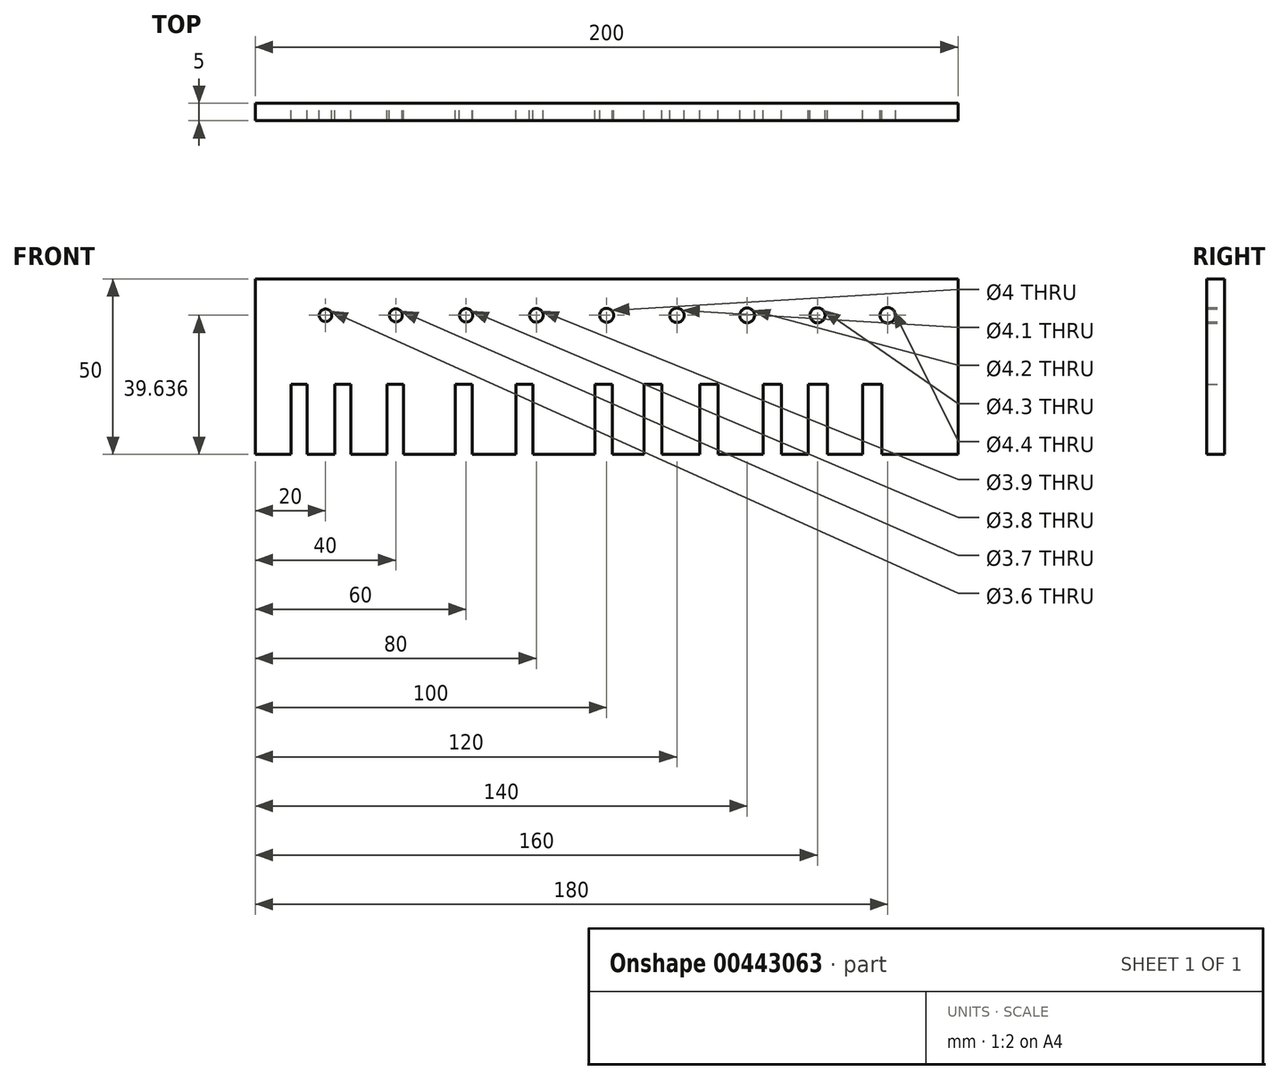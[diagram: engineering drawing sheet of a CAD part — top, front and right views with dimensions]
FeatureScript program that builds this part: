
annotation { "Feature Type Name" : "Feature", "Feature Type Description" : "" }
export const myFeature = defineFeature(function(context is Context, id is Id, definition is map)
    precondition{}
    {
        {
            var Q0;
            Q0=qCreatedBy(makeId("Front.planeOp"),FACE);
            var sketch = newSketch(context, id + "F0", { "sketchPlane" : qUnion([Q0])});
            skLineSegment(sketch, "E0.bottom", {"start": v(100, 25) * mm, "end": v(-100, 25) * mm});
            skLineSegment(sketch, "E0.top", {"start": v(100, -25) * mm, "end": v(-100, -25) * mm});
            skLineSegment(sketch, "E0.left", {"start": v(100, 25) * mm, "end": v(100, -25) * mm});
            skLineSegment(sketch, "E0.right", {"start": v(-100, 25) * mm, "end": v(-100, -25) * mm});
            skPoint(sketch, "E0.middle", {"position": v(0, 0) * mm});
            skLineSegment(sketch, "E1.bottom", {"start": v(-3.33, -25) * mm, "end": v(1.67, -25) * mm});
            skLineSegment(sketch, "E1.top", {"start": v(-3.33, -5) * mm, "end": v(1.67, -5) * mm});
            skLineSegment(sketch, "E1.left", {"start": v(-3.33, -25) * mm, "end": v(-3.33, -5) * mm});
            skLineSegment(sketch, "E1.right", {"start": v(1.67, -25) * mm, "end": v(1.67, -5) * mm});
            skLineSegment(sketch, "E2.bottom", {"start": v(-20.96, -25) * mm, "end": v(-25.86, -25) * mm});
            skLineSegment(sketch, "E2.top", {"start": v(-20.96, -5) * mm, "end": v(-25.86, -5) * mm});
            skLineSegment(sketch, "E2.left", {"start": v(-20.96, -25) * mm, "end": v(-20.96, -5) * mm});
            skLineSegment(sketch, "E2.right", {"start": v(-25.86, -25) * mm, "end": v(-25.86, -5) * mm});
            skLineSegment(sketch, "E3.bottom", {"start": v(-38.22, -25) * mm, "end": v(-43.02, -25) * mm});
            skLineSegment(sketch, "E3.top", {"start": v(-38.22, -5) * mm, "end": v(-43.02, -5) * mm});
            skLineSegment(sketch, "E3.left", {"start": v(-38.22, -25) * mm, "end": v(-38.22, -5) * mm});
            skLineSegment(sketch, "E3.right", {"start": v(-43.02, -25) * mm, "end": v(-43.02, -5) * mm});
            skLineSegment(sketch, "E4.bottom", {"start": v(-57.85, -25) * mm, "end": v(-62.55, -25) * mm});
            skLineSegment(sketch, "E4.top", {"start": v(-57.85, -5) * mm, "end": v(-62.55, -5) * mm});
            skLineSegment(sketch, "E4.left", {"start": v(-57.85, -25) * mm, "end": v(-57.85, -5) * mm});
            skLineSegment(sketch, "E4.right", {"start": v(-62.55, -25) * mm, "end": v(-62.55, -5) * mm});
            skLineSegment(sketch, "E5.bottom", {"start": v(-72.75, -25) * mm, "end": v(-77.35, -25) * mm});
            skLineSegment(sketch, "E5.top", {"start": v(-72.75, -5) * mm, "end": v(-77.35, -5) * mm});
            skLineSegment(sketch, "E5.left", {"start": v(-72.75, -25) * mm, "end": v(-72.75, -5) * mm});
            skLineSegment(sketch, "E5.right", {"start": v(-77.35, -25) * mm, "end": v(-77.35, -5) * mm});
            skLineSegment(sketch, "E6.bottom", {"start": v(-85.3, -25) * mm, "end": v(-89.8, -25) * mm});
            skLineSegment(sketch, "E6.top", {"start": v(-85.3, -5) * mm, "end": v(-89.8, -5) * mm});
            skLineSegment(sketch, "E6.left", {"start": v(-85.3, -25) * mm, "end": v(-85.3, -5) * mm});
            skLineSegment(sketch, "E6.right", {"start": v(-89.8, -25) * mm, "end": v(-89.8, -5) * mm});
            skLineSegment(sketch, "E7.bottom", {"start": v(10.61, -25) * mm, "end": v(15.71, -25) * mm});
            skLineSegment(sketch, "E7.top", {"start": v(10.61, -5) * mm, "end": v(15.71, -5) * mm});
            skLineSegment(sketch, "E7.left", {"start": v(10.61, -25) * mm, "end": v(10.61, -5) * mm});
            skLineSegment(sketch, "E7.right", {"start": v(15.71, -25) * mm, "end": v(15.71, -5) * mm});
            skLineSegment(sketch, "E8.bottom", {"start": v(26.49, -25) * mm, "end": v(31.69, -25) * mm});
            skLineSegment(sketch, "E8.top", {"start": v(26.49, -5) * mm, "end": v(31.69, -5) * mm});
            skLineSegment(sketch, "E8.left", {"start": v(26.49, -25) * mm, "end": v(26.49, -5) * mm});
            skLineSegment(sketch, "E8.right", {"start": v(31.69, -25) * mm, "end": v(31.69, -5) * mm});
            skLineSegment(sketch, "E9.bottom", {"start": v(44.5, -25) * mm, "end": v(49.8, -25) * mm});
            skLineSegment(sketch, "E9.top", {"start": v(44.5, -5) * mm, "end": v(49.8, -5) * mm});
            skLineSegment(sketch, "E9.left", {"start": v(44.5, -25) * mm, "end": v(44.5, -5) * mm});
            skLineSegment(sketch, "E9.right", {"start": v(49.8, -25) * mm, "end": v(49.8, -5) * mm});
            skLineSegment(sketch, "E10.bottom", {"start": v(57.38, -25) * mm, "end": v(62.78, -25) * mm});
            skLineSegment(sketch, "E10.top", {"start": v(57.38, -5) * mm, "end": v(62.78, -5) * mm});
            skLineSegment(sketch, "E10.left", {"start": v(57.38, -25) * mm, "end": v(57.38, -5) * mm});
            skLineSegment(sketch, "E10.right", {"start": v(62.78, -25) * mm, "end": v(62.78, -5) * mm});
            skLineSegment(sketch, "E11.bottom", {"start": v(72.83, -25) * mm, "end": v(78.33, -25) * mm});
            skLineSegment(sketch, "E11.top", {"start": v(72.83, -5) * mm, "end": v(78.33, -5) * mm});
            skLineSegment(sketch, "E11.left", {"start": v(72.83, -25) * mm, "end": v(72.83, -5) * mm});
            skLineSegment(sketch, "E11.right", {"start": v(78.33, -25) * mm, "end": v(78.33, -5) * mm});
            skSolve(sketch);
        }
        {
            var Q0;
            Q0=makeQuery(id+"F0.imprint","IMPRINT",FACE,{"disambiguationData":[TD([[makeQuery(id+"F0.imprint","IMPRINT",EDGE,{"derivedFrom":sQuery(id+"F0.wireOp",EDGE,"E0.bottom")}),1.0]])]});
            extrude(context, id + "F1", {"entities" : qUnion([Q0]), "depth" : 5 * mm});
        }
        {
            var Q0;
            Q0=qCreatedBy(makeId("Front.planeOp"),FACE);
            var sketch = newSketch(context, id + "F2", { "sketchPlane" : qUnion([Q0])});
            skPoint(sketch, "E12", {"position": v(0, 14.64) * mm});
            skPoint(sketch, "E13.1.0.0", {"position": v(20, 14.64) * mm});
            skPoint(sketch, "E13.2.0.0", {"position": v(40, 14.64) * mm});
            skPoint(sketch, "E13.3.0.0", {"position": v(60, 14.64) * mm});
            skPoint(sketch, "E13.4.0.0", {"position": v(80, 14.64) * mm});
            skLineSegment(sketch, "E13.direction1", {"start": v(0, 14.64) * mm, "end": v(20, 14.64) * mm, "construction": true});
            skPoint(sketch, "E14.1.0.0", {"position": v(-20, 14.64) * mm});
            skPoint(sketch, "E14.2.0.0", {"position": v(-40, 14.64) * mm});
            skPoint(sketch, "E14.3.0.0", {"position": v(-60, 14.64) * mm});
            skPoint(sketch, "E14.4.0.0", {"position": v(-80, 14.64) * mm});
            skLineSegment(sketch, "E14.direction1", {"start": v(0, 14.64) * mm, "end": v(-20, 14.64) * mm, "construction": true});
            skSolve(sketch);
        }
        {
            var Q0;
            Q0=sQuery(id+"F2.wireOp",VERTEX,"E12");
            var Q1;
            Q1=makeQuery(id+"F1.opExtrude","SWEPT_BODY",BODY,{"disambiguationData":[OSD([sQuery(id+"F0.wireOp",EDGE,"E0.bottom"),sQuery(id+"F0.wireOp",EDGE,"E0.top"),sQuery(id+"F0.wireOp",EDGE,"E0.left"),sQuery(id+"F0.wireOp",EDGE,"E0.right"),sQuery(id+"F0.wireOp",EDGE,"E1.top"),sQuery(id+"F0.wireOp",EDGE,"E1.left"),sQuery(id+"F0.wireOp",EDGE,"E1.right"),sQuery(id+"F0.wireOp",EDGE,"E2.top"),sQuery(id+"F0.wireOp",EDGE,"E2.left"),sQuery(id+"F0.wireOp",EDGE,"E2.right"),sQuery(id+"F0.wireOp",EDGE,"E3.top"),sQuery(id+"F0.wireOp",EDGE,"E3.left"),sQuery(id+"F0.wireOp",EDGE,"E3.right"),sQuery(id+"F0.wireOp",EDGE,"E4.top"),sQuery(id+"F0.wireOp",EDGE,"E4.left"),sQuery(id+"F0.wireOp",EDGE,"E4.right"),sQuery(id+"F0.wireOp",EDGE,"E5.top"),sQuery(id+"F0.wireOp",EDGE,"E5.left"),sQuery(id+"F0.wireOp",EDGE,"E5.right"),sQuery(id+"F0.wireOp",EDGE,"E6.top"),sQuery(id+"F0.wireOp",EDGE,"E6.left"),sQuery(id+"F0.wireOp",EDGE,"E6.right"),sQuery(id+"F0.wireOp",EDGE,"E7.top"),sQuery(id+"F0.wireOp",EDGE,"E7.left"),sQuery(id+"F0.wireOp",EDGE,"E7.right"),sQuery(id+"F0.wireOp",EDGE,"E8.top"),sQuery(id+"F0.wireOp",EDGE,"E8.left"),sQuery(id+"F0.wireOp",EDGE,"E8.right"),sQuery(id+"F0.wireOp",EDGE,"E9.top"),sQuery(id+"F0.wireOp",EDGE,"E9.left"),sQuery(id+"F0.wireOp",EDGE,"E9.right"),sQuery(id+"F0.wireOp",EDGE,"E10.top"),sQuery(id+"F0.wireOp",EDGE,"E10.left"),sQuery(id+"F0.wireOp",EDGE,"E10.right"),sQuery(id+"F0.wireOp",EDGE,"E11.top"),sQuery(id+"F0.wireOp",EDGE,"E11.left"),sQuery(id+"F0.wireOp",EDGE,"E11.right")])]});
            hole(context, id + "F3", {"style" : HoleStyle.SIMPLE, "endStyle" : HoleEndStyle.THROUGH, "oppositeDirection" : true, "holeDiameter" : 4 * mm, "isTappedThrough" : true, "tappedDepth" : 12 * mm, "tapClearance" : 3, "locations" : qUnion([Q0]), "scope" : qUnion([Q1])});
        }
        {
            var Q0;
            Q0=sQuery(id+"F2.wireOp",VERTEX,"E13.1.0.0");
            var Q1;
            Q1=makeQuery(id+"F1.opExtrude","SWEPT_BODY",BODY,{"disambiguationData":[OSD([sQuery(id+"F0.wireOp",EDGE,"E0.bottom"),sQuery(id+"F0.wireOp",EDGE,"E0.top"),sQuery(id+"F0.wireOp",EDGE,"E0.left"),sQuery(id+"F0.wireOp",EDGE,"E0.right"),sQuery(id+"F0.wireOp",EDGE,"E1.top"),sQuery(id+"F0.wireOp",EDGE,"E1.left"),sQuery(id+"F0.wireOp",EDGE,"E1.right"),sQuery(id+"F0.wireOp",EDGE,"E2.top"),sQuery(id+"F0.wireOp",EDGE,"E2.left"),sQuery(id+"F0.wireOp",EDGE,"E2.right"),sQuery(id+"F0.wireOp",EDGE,"E3.top"),sQuery(id+"F0.wireOp",EDGE,"E3.left"),sQuery(id+"F0.wireOp",EDGE,"E3.right"),sQuery(id+"F0.wireOp",EDGE,"E4.top"),sQuery(id+"F0.wireOp",EDGE,"E4.left"),sQuery(id+"F0.wireOp",EDGE,"E4.right"),sQuery(id+"F0.wireOp",EDGE,"E5.top"),sQuery(id+"F0.wireOp",EDGE,"E5.left"),sQuery(id+"F0.wireOp",EDGE,"E5.right"),sQuery(id+"F0.wireOp",EDGE,"E6.top"),sQuery(id+"F0.wireOp",EDGE,"E6.left"),sQuery(id+"F0.wireOp",EDGE,"E6.right"),sQuery(id+"F0.wireOp",EDGE,"E7.top"),sQuery(id+"F0.wireOp",EDGE,"E7.left"),sQuery(id+"F0.wireOp",EDGE,"E7.right"),sQuery(id+"F0.wireOp",EDGE,"E8.top"),sQuery(id+"F0.wireOp",EDGE,"E8.left"),sQuery(id+"F0.wireOp",EDGE,"E8.right"),sQuery(id+"F0.wireOp",EDGE,"E9.top"),sQuery(id+"F0.wireOp",EDGE,"E9.left"),sQuery(id+"F0.wireOp",EDGE,"E9.right"),sQuery(id+"F0.wireOp",EDGE,"E10.top"),sQuery(id+"F0.wireOp",EDGE,"E10.left"),sQuery(id+"F0.wireOp",EDGE,"E10.right"),sQuery(id+"F0.wireOp",EDGE,"E11.top"),sQuery(id+"F0.wireOp",EDGE,"E11.left"),sQuery(id+"F0.wireOp",EDGE,"E11.right")])]});
            hole(context, id + "F4", {"style" : HoleStyle.SIMPLE, "endStyle" : HoleEndStyle.THROUGH, "oppositeDirection" : true, "holeDiameter" : 4.1 * mm, "isTappedThrough" : true, "tappedDepth" : 12 * mm, "tapClearance" : 3, "locations" : qUnion([Q0]), "scope" : qUnion([Q1])});
        }
        {
            var Q0;
            Q0=sQuery(id+"F2.wireOp",VERTEX,"E13.2.0.0");
            var Q1;
            Q1=makeQuery(id+"F1.opExtrude","SWEPT_BODY",BODY,{"disambiguationData":[OSD([sQuery(id+"F0.wireOp",EDGE,"E0.bottom"),sQuery(id+"F0.wireOp",EDGE,"E0.top"),sQuery(id+"F0.wireOp",EDGE,"E0.left"),sQuery(id+"F0.wireOp",EDGE,"E0.right"),sQuery(id+"F0.wireOp",EDGE,"E1.top"),sQuery(id+"F0.wireOp",EDGE,"E1.left"),sQuery(id+"F0.wireOp",EDGE,"E1.right"),sQuery(id+"F0.wireOp",EDGE,"E2.top"),sQuery(id+"F0.wireOp",EDGE,"E2.left"),sQuery(id+"F0.wireOp",EDGE,"E2.right"),sQuery(id+"F0.wireOp",EDGE,"E3.top"),sQuery(id+"F0.wireOp",EDGE,"E3.left"),sQuery(id+"F0.wireOp",EDGE,"E3.right"),sQuery(id+"F0.wireOp",EDGE,"E4.top"),sQuery(id+"F0.wireOp",EDGE,"E4.left"),sQuery(id+"F0.wireOp",EDGE,"E4.right"),sQuery(id+"F0.wireOp",EDGE,"E5.top"),sQuery(id+"F0.wireOp",EDGE,"E5.left"),sQuery(id+"F0.wireOp",EDGE,"E5.right"),sQuery(id+"F0.wireOp",EDGE,"E6.top"),sQuery(id+"F0.wireOp",EDGE,"E6.left"),sQuery(id+"F0.wireOp",EDGE,"E6.right"),sQuery(id+"F0.wireOp",EDGE,"E7.top"),sQuery(id+"F0.wireOp",EDGE,"E7.left"),sQuery(id+"F0.wireOp",EDGE,"E7.right"),sQuery(id+"F0.wireOp",EDGE,"E8.top"),sQuery(id+"F0.wireOp",EDGE,"E8.left"),sQuery(id+"F0.wireOp",EDGE,"E8.right"),sQuery(id+"F0.wireOp",EDGE,"E9.top"),sQuery(id+"F0.wireOp",EDGE,"E9.left"),sQuery(id+"F0.wireOp",EDGE,"E9.right"),sQuery(id+"F0.wireOp",EDGE,"E10.top"),sQuery(id+"F0.wireOp",EDGE,"E10.left"),sQuery(id+"F0.wireOp",EDGE,"E10.right"),sQuery(id+"F0.wireOp",EDGE,"E11.top"),sQuery(id+"F0.wireOp",EDGE,"E11.left"),sQuery(id+"F0.wireOp",EDGE,"E11.right")])]});
            hole(context, id + "F5", {"style" : HoleStyle.SIMPLE, "endStyle" : HoleEndStyle.THROUGH, "oppositeDirection" : true, "holeDiameter" : 4.2 * mm, "isTappedThrough" : true, "tappedDepth" : 12 * mm, "tapClearance" : 3, "locations" : qUnion([Q0]), "scope" : qUnion([Q1])});
        }
        {
            var Q0;
            Q0=sQuery(id+"F2.wireOp",VERTEX,"E13.3.0.0");
            var Q1;
            Q1=makeQuery(id+"F1.opExtrude","SWEPT_BODY",BODY,{"disambiguationData":[OSD([sQuery(id+"F0.wireOp",EDGE,"E0.bottom"),sQuery(id+"F0.wireOp",EDGE,"E0.top"),sQuery(id+"F0.wireOp",EDGE,"E0.left"),sQuery(id+"F0.wireOp",EDGE,"E0.right"),sQuery(id+"F0.wireOp",EDGE,"E1.top"),sQuery(id+"F0.wireOp",EDGE,"E1.left"),sQuery(id+"F0.wireOp",EDGE,"E1.right"),sQuery(id+"F0.wireOp",EDGE,"E2.top"),sQuery(id+"F0.wireOp",EDGE,"E2.left"),sQuery(id+"F0.wireOp",EDGE,"E2.right"),sQuery(id+"F0.wireOp",EDGE,"E3.top"),sQuery(id+"F0.wireOp",EDGE,"E3.left"),sQuery(id+"F0.wireOp",EDGE,"E3.right"),sQuery(id+"F0.wireOp",EDGE,"E4.top"),sQuery(id+"F0.wireOp",EDGE,"E4.left"),sQuery(id+"F0.wireOp",EDGE,"E4.right"),sQuery(id+"F0.wireOp",EDGE,"E5.top"),sQuery(id+"F0.wireOp",EDGE,"E5.left"),sQuery(id+"F0.wireOp",EDGE,"E5.right"),sQuery(id+"F0.wireOp",EDGE,"E6.top"),sQuery(id+"F0.wireOp",EDGE,"E6.left"),sQuery(id+"F0.wireOp",EDGE,"E6.right"),sQuery(id+"F0.wireOp",EDGE,"E7.top"),sQuery(id+"F0.wireOp",EDGE,"E7.left"),sQuery(id+"F0.wireOp",EDGE,"E7.right"),sQuery(id+"F0.wireOp",EDGE,"E8.top"),sQuery(id+"F0.wireOp",EDGE,"E8.left"),sQuery(id+"F0.wireOp",EDGE,"E8.right"),sQuery(id+"F0.wireOp",EDGE,"E9.top"),sQuery(id+"F0.wireOp",EDGE,"E9.left"),sQuery(id+"F0.wireOp",EDGE,"E9.right"),sQuery(id+"F0.wireOp",EDGE,"E10.top"),sQuery(id+"F0.wireOp",EDGE,"E10.left"),sQuery(id+"F0.wireOp",EDGE,"E10.right"),sQuery(id+"F0.wireOp",EDGE,"E11.top"),sQuery(id+"F0.wireOp",EDGE,"E11.left"),sQuery(id+"F0.wireOp",EDGE,"E11.right")])]});
            hole(context, id + "F6", {"style" : HoleStyle.SIMPLE, "endStyle" : HoleEndStyle.THROUGH, "oppositeDirection" : true, "holeDiameter" : 4.3 * mm, "isTappedThrough" : true, "tappedDepth" : 12 * mm, "tapClearance" : 3, "locations" : qUnion([Q0]), "scope" : qUnion([Q1])});
        }
        {
            var Q0;
            Q0=sQuery(id+"F2.wireOp",VERTEX,"E13.4.0.0");
            var Q1;
            Q1=makeQuery(id+"F1.opExtrude","SWEPT_BODY",BODY,{"disambiguationData":[OSD([sQuery(id+"F0.wireOp",EDGE,"E0.bottom"),sQuery(id+"F0.wireOp",EDGE,"E0.top"),sQuery(id+"F0.wireOp",EDGE,"E0.left"),sQuery(id+"F0.wireOp",EDGE,"E0.right"),sQuery(id+"F0.wireOp",EDGE,"E1.top"),sQuery(id+"F0.wireOp",EDGE,"E1.left"),sQuery(id+"F0.wireOp",EDGE,"E1.right"),sQuery(id+"F0.wireOp",EDGE,"E2.top"),sQuery(id+"F0.wireOp",EDGE,"E2.left"),sQuery(id+"F0.wireOp",EDGE,"E2.right"),sQuery(id+"F0.wireOp",EDGE,"E3.top"),sQuery(id+"F0.wireOp",EDGE,"E3.left"),sQuery(id+"F0.wireOp",EDGE,"E3.right"),sQuery(id+"F0.wireOp",EDGE,"E4.top"),sQuery(id+"F0.wireOp",EDGE,"E4.left"),sQuery(id+"F0.wireOp",EDGE,"E4.right"),sQuery(id+"F0.wireOp",EDGE,"E5.top"),sQuery(id+"F0.wireOp",EDGE,"E5.left"),sQuery(id+"F0.wireOp",EDGE,"E5.right"),sQuery(id+"F0.wireOp",EDGE,"E6.top"),sQuery(id+"F0.wireOp",EDGE,"E6.left"),sQuery(id+"F0.wireOp",EDGE,"E6.right"),sQuery(id+"F0.wireOp",EDGE,"E7.top"),sQuery(id+"F0.wireOp",EDGE,"E7.left"),sQuery(id+"F0.wireOp",EDGE,"E7.right"),sQuery(id+"F0.wireOp",EDGE,"E8.top"),sQuery(id+"F0.wireOp",EDGE,"E8.left"),sQuery(id+"F0.wireOp",EDGE,"E8.right"),sQuery(id+"F0.wireOp",EDGE,"E9.top"),sQuery(id+"F0.wireOp",EDGE,"E9.left"),sQuery(id+"F0.wireOp",EDGE,"E9.right"),sQuery(id+"F0.wireOp",EDGE,"E10.top"),sQuery(id+"F0.wireOp",EDGE,"E10.left"),sQuery(id+"F0.wireOp",EDGE,"E10.right"),sQuery(id+"F0.wireOp",EDGE,"E11.top"),sQuery(id+"F0.wireOp",EDGE,"E11.left"),sQuery(id+"F0.wireOp",EDGE,"E11.right")])]});
            hole(context, id + "F7", {"style" : HoleStyle.SIMPLE, "endStyle" : HoleEndStyle.THROUGH, "oppositeDirection" : true, "holeDiameter" : 4.4 * mm, "isTappedThrough" : true, "tappedDepth" : 12 * mm, "tapClearance" : 3, "locations" : qUnion([Q0]), "scope" : qUnion([Q1])});
        }
        {
            var Q0;
            Q0=sQuery(id+"F2.wireOp",VERTEX,"E14.1.0.0");
            var Q1;
            Q1=makeQuery(id+"F1.opExtrude","SWEPT_BODY",BODY,{"disambiguationData":[OSD([sQuery(id+"F0.wireOp",EDGE,"E0.bottom"),sQuery(id+"F0.wireOp",EDGE,"E0.top"),sQuery(id+"F0.wireOp",EDGE,"E0.left"),sQuery(id+"F0.wireOp",EDGE,"E0.right"),sQuery(id+"F0.wireOp",EDGE,"E1.top"),sQuery(id+"F0.wireOp",EDGE,"E1.left"),sQuery(id+"F0.wireOp",EDGE,"E1.right"),sQuery(id+"F0.wireOp",EDGE,"E2.top"),sQuery(id+"F0.wireOp",EDGE,"E2.left"),sQuery(id+"F0.wireOp",EDGE,"E2.right"),sQuery(id+"F0.wireOp",EDGE,"E3.top"),sQuery(id+"F0.wireOp",EDGE,"E3.left"),sQuery(id+"F0.wireOp",EDGE,"E3.right"),sQuery(id+"F0.wireOp",EDGE,"E4.top"),sQuery(id+"F0.wireOp",EDGE,"E4.left"),sQuery(id+"F0.wireOp",EDGE,"E4.right"),sQuery(id+"F0.wireOp",EDGE,"E5.top"),sQuery(id+"F0.wireOp",EDGE,"E5.left"),sQuery(id+"F0.wireOp",EDGE,"E5.right"),sQuery(id+"F0.wireOp",EDGE,"E6.top"),sQuery(id+"F0.wireOp",EDGE,"E6.left"),sQuery(id+"F0.wireOp",EDGE,"E6.right"),sQuery(id+"F0.wireOp",EDGE,"E7.top"),sQuery(id+"F0.wireOp",EDGE,"E7.left"),sQuery(id+"F0.wireOp",EDGE,"E7.right"),sQuery(id+"F0.wireOp",EDGE,"E8.top"),sQuery(id+"F0.wireOp",EDGE,"E8.left"),sQuery(id+"F0.wireOp",EDGE,"E8.right"),sQuery(id+"F0.wireOp",EDGE,"E9.top"),sQuery(id+"F0.wireOp",EDGE,"E9.left"),sQuery(id+"F0.wireOp",EDGE,"E9.right"),sQuery(id+"F0.wireOp",EDGE,"E10.top"),sQuery(id+"F0.wireOp",EDGE,"E10.left"),sQuery(id+"F0.wireOp",EDGE,"E10.right"),sQuery(id+"F0.wireOp",EDGE,"E11.top"),sQuery(id+"F0.wireOp",EDGE,"E11.left"),sQuery(id+"F0.wireOp",EDGE,"E11.right")])]});
            hole(context, id + "F8", {"style" : HoleStyle.SIMPLE, "endStyle" : HoleEndStyle.THROUGH, "oppositeDirection" : true, "holeDiameter" : 3.9 * mm, "isTappedThrough" : true, "tappedDepth" : 12 * mm, "tapClearance" : 3, "locations" : qUnion([Q0]), "scope" : qUnion([Q1])});
        }
        {
            var Q0;
            Q0=sQuery(id+"F2.wireOp",VERTEX,"E14.2.0.0");
            var Q1;
            Q1=makeQuery(id+"F1.opExtrude","SWEPT_BODY",BODY,{"disambiguationData":[OSD([sQuery(id+"F0.wireOp",EDGE,"E0.bottom"),sQuery(id+"F0.wireOp",EDGE,"E0.top"),sQuery(id+"F0.wireOp",EDGE,"E0.left"),sQuery(id+"F0.wireOp",EDGE,"E0.right"),sQuery(id+"F0.wireOp",EDGE,"E1.top"),sQuery(id+"F0.wireOp",EDGE,"E1.left"),sQuery(id+"F0.wireOp",EDGE,"E1.right"),sQuery(id+"F0.wireOp",EDGE,"E2.top"),sQuery(id+"F0.wireOp",EDGE,"E2.left"),sQuery(id+"F0.wireOp",EDGE,"E2.right"),sQuery(id+"F0.wireOp",EDGE,"E3.top"),sQuery(id+"F0.wireOp",EDGE,"E3.left"),sQuery(id+"F0.wireOp",EDGE,"E3.right"),sQuery(id+"F0.wireOp",EDGE,"E4.top"),sQuery(id+"F0.wireOp",EDGE,"E4.left"),sQuery(id+"F0.wireOp",EDGE,"E4.right"),sQuery(id+"F0.wireOp",EDGE,"E5.top"),sQuery(id+"F0.wireOp",EDGE,"E5.left"),sQuery(id+"F0.wireOp",EDGE,"E5.right"),sQuery(id+"F0.wireOp",EDGE,"E6.top"),sQuery(id+"F0.wireOp",EDGE,"E6.left"),sQuery(id+"F0.wireOp",EDGE,"E6.right"),sQuery(id+"F0.wireOp",EDGE,"E7.top"),sQuery(id+"F0.wireOp",EDGE,"E7.left"),sQuery(id+"F0.wireOp",EDGE,"E7.right"),sQuery(id+"F0.wireOp",EDGE,"E8.top"),sQuery(id+"F0.wireOp",EDGE,"E8.left"),sQuery(id+"F0.wireOp",EDGE,"E8.right"),sQuery(id+"F0.wireOp",EDGE,"E9.top"),sQuery(id+"F0.wireOp",EDGE,"E9.left"),sQuery(id+"F0.wireOp",EDGE,"E9.right"),sQuery(id+"F0.wireOp",EDGE,"E10.top"),sQuery(id+"F0.wireOp",EDGE,"E10.left"),sQuery(id+"F0.wireOp",EDGE,"E10.right"),sQuery(id+"F0.wireOp",EDGE,"E11.top"),sQuery(id+"F0.wireOp",EDGE,"E11.left"),sQuery(id+"F0.wireOp",EDGE,"E11.right")])]});
            hole(context, id + "F9", {"style" : HoleStyle.SIMPLE, "endStyle" : HoleEndStyle.THROUGH, "oppositeDirection" : true, "holeDiameter" : 3.8 * mm, "isTappedThrough" : true, "tappedDepth" : 12 * mm, "tapClearance" : 3, "locations" : qUnion([Q0]), "scope" : qUnion([Q1])});
        }
        {
            var Q0;
            Q0=sQuery(id+"F2.wireOp",VERTEX,"E14.3.0.0");
            var Q1;
            Q1=makeQuery(id+"F1.opExtrude","SWEPT_BODY",BODY,{"disambiguationData":[OSD([sQuery(id+"F0.wireOp",EDGE,"E0.bottom"),sQuery(id+"F0.wireOp",EDGE,"E0.top"),sQuery(id+"F0.wireOp",EDGE,"E0.left"),sQuery(id+"F0.wireOp",EDGE,"E0.right"),sQuery(id+"F0.wireOp",EDGE,"E1.top"),sQuery(id+"F0.wireOp",EDGE,"E1.left"),sQuery(id+"F0.wireOp",EDGE,"E1.right"),sQuery(id+"F0.wireOp",EDGE,"E2.top"),sQuery(id+"F0.wireOp",EDGE,"E2.left"),sQuery(id+"F0.wireOp",EDGE,"E2.right"),sQuery(id+"F0.wireOp",EDGE,"E3.top"),sQuery(id+"F0.wireOp",EDGE,"E3.left"),sQuery(id+"F0.wireOp",EDGE,"E3.right"),sQuery(id+"F0.wireOp",EDGE,"E4.top"),sQuery(id+"F0.wireOp",EDGE,"E4.left"),sQuery(id+"F0.wireOp",EDGE,"E4.right"),sQuery(id+"F0.wireOp",EDGE,"E5.top"),sQuery(id+"F0.wireOp",EDGE,"E5.left"),sQuery(id+"F0.wireOp",EDGE,"E5.right"),sQuery(id+"F0.wireOp",EDGE,"E6.top"),sQuery(id+"F0.wireOp",EDGE,"E6.left"),sQuery(id+"F0.wireOp",EDGE,"E6.right"),sQuery(id+"F0.wireOp",EDGE,"E7.top"),sQuery(id+"F0.wireOp",EDGE,"E7.left"),sQuery(id+"F0.wireOp",EDGE,"E7.right"),sQuery(id+"F0.wireOp",EDGE,"E8.top"),sQuery(id+"F0.wireOp",EDGE,"E8.left"),sQuery(id+"F0.wireOp",EDGE,"E8.right"),sQuery(id+"F0.wireOp",EDGE,"E9.top"),sQuery(id+"F0.wireOp",EDGE,"E9.left"),sQuery(id+"F0.wireOp",EDGE,"E9.right"),sQuery(id+"F0.wireOp",EDGE,"E10.top"),sQuery(id+"F0.wireOp",EDGE,"E10.left"),sQuery(id+"F0.wireOp",EDGE,"E10.right"),sQuery(id+"F0.wireOp",EDGE,"E11.top"),sQuery(id+"F0.wireOp",EDGE,"E11.left"),sQuery(id+"F0.wireOp",EDGE,"E11.right")])]});
            hole(context, id + "F10", {"style" : HoleStyle.SIMPLE, "endStyle" : HoleEndStyle.THROUGH, "oppositeDirection" : true, "holeDiameter" : 3.7 * mm, "isTappedThrough" : true, "tappedDepth" : 12 * mm, "tapClearance" : 3, "locations" : qUnion([Q0]), "scope" : qUnion([Q1])});
        }
        {
            var Q0;
            Q0=sQuery(id+"F2.wireOp",VERTEX,"E14.4.0.0");
            var Q1;
            Q1=makeQuery(id+"F1.opExtrude","SWEPT_BODY",BODY,{"disambiguationData":[OSD([sQuery(id+"F0.wireOp",EDGE,"E0.bottom"),sQuery(id+"F0.wireOp",EDGE,"E0.top"),sQuery(id+"F0.wireOp",EDGE,"E0.left"),sQuery(id+"F0.wireOp",EDGE,"E0.right"),sQuery(id+"F0.wireOp",EDGE,"E1.top"),sQuery(id+"F0.wireOp",EDGE,"E1.left"),sQuery(id+"F0.wireOp",EDGE,"E1.right"),sQuery(id+"F0.wireOp",EDGE,"E2.top"),sQuery(id+"F0.wireOp",EDGE,"E2.left"),sQuery(id+"F0.wireOp",EDGE,"E2.right"),sQuery(id+"F0.wireOp",EDGE,"E3.top"),sQuery(id+"F0.wireOp",EDGE,"E3.left"),sQuery(id+"F0.wireOp",EDGE,"E3.right"),sQuery(id+"F0.wireOp",EDGE,"E4.top"),sQuery(id+"F0.wireOp",EDGE,"E4.left"),sQuery(id+"F0.wireOp",EDGE,"E4.right"),sQuery(id+"F0.wireOp",EDGE,"E5.top"),sQuery(id+"F0.wireOp",EDGE,"E5.left"),sQuery(id+"F0.wireOp",EDGE,"E5.right"),sQuery(id+"F0.wireOp",EDGE,"E6.top"),sQuery(id+"F0.wireOp",EDGE,"E6.left"),sQuery(id+"F0.wireOp",EDGE,"E6.right"),sQuery(id+"F0.wireOp",EDGE,"E7.top"),sQuery(id+"F0.wireOp",EDGE,"E7.left"),sQuery(id+"F0.wireOp",EDGE,"E7.right"),sQuery(id+"F0.wireOp",EDGE,"E8.top"),sQuery(id+"F0.wireOp",EDGE,"E8.left"),sQuery(id+"F0.wireOp",EDGE,"E8.right"),sQuery(id+"F0.wireOp",EDGE,"E9.top"),sQuery(id+"F0.wireOp",EDGE,"E9.left"),sQuery(id+"F0.wireOp",EDGE,"E9.right"),sQuery(id+"F0.wireOp",EDGE,"E10.top"),sQuery(id+"F0.wireOp",EDGE,"E10.left"),sQuery(id+"F0.wireOp",EDGE,"E10.right"),sQuery(id+"F0.wireOp",EDGE,"E11.top"),sQuery(id+"F0.wireOp",EDGE,"E11.left"),sQuery(id+"F0.wireOp",EDGE,"E11.right")])]});
            hole(context, id + "F11", {"style" : HoleStyle.SIMPLE, "endStyle" : HoleEndStyle.THROUGH, "oppositeDirection" : true, "holeDiameter" : 3.6 * mm, "isTappedThrough" : true, "tappedDepth" : 12 * mm, "tapClearance" : 3, "locations" : qUnion([Q0]), "scope" : qUnion([Q1])});
        }
    });
